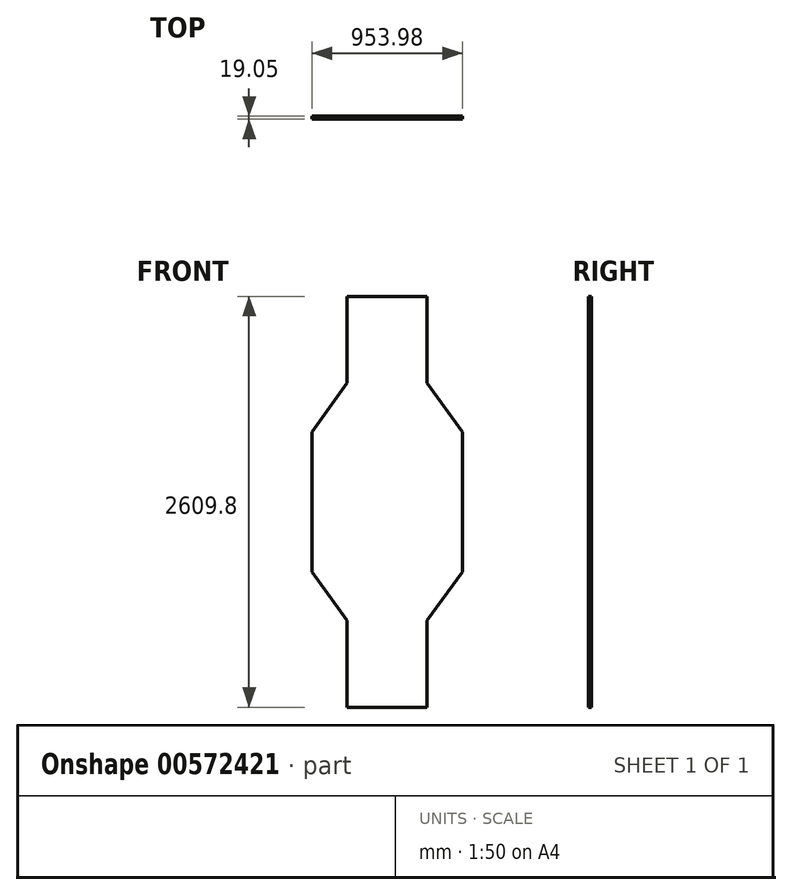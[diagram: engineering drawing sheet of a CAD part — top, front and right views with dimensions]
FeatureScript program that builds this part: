
annotation { "Feature Type Name" : "Feature", "Feature Type Description" : "" }
export const myFeature = defineFeature(function(context is Context, id is Id, definition is map)
    precondition{}
    {
        {
            var Q0;
            Q0=qCreatedBy(makeId("Front.planeOp"),FACE);
            var sketch = newSketch(context, id + "F0", { "sketchPlane" : qUnion([Q0])});
            skLineSegment(sketch, "E0", {"start": v(-515.56, -2037.32) * mm, "end": v(-292.57, -2346.25) * mm});
            skLineSegment(sketch, "E1", {"start": v(-292.57, -2346.25) * mm, "end": v(-292.57, -2897.72) * mm});
            skLineSegment(sketch, "E2", {"start": v(-292.57, -2897.72) * mm, "end": v(215.43, -2897.72) * mm});
            skLineSegment(sketch, "E3", {"start": v(215.43, -2897.72) * mm, "end": v(215.43, -2346.25) * mm});
            skPoint(sketch, "E4.startSnap0", {"position": v(-38.57, -2897.72) * mm});
            skLineSegment(sketch, "E5", {"start": v(-515.56, -2037.32) * mm, "end": v(-515.56, -1148.32) * mm});
            skLineSegment(sketch, "E6.MirrorCS", {"start": v(438.42, -2037.32) * mm, "end": v(438.42, -1148.32) * mm});
            skLineSegment(sketch, "E7.MirrorCS", {"start": v(438.42, -2037.32) * mm, "end": v(215.43, -2346.25) * mm});
            skLineSegment(sketch, "E8.MirrorCS", {"start": v(-515.56, -1148.32) * mm, "end": v(-292.57, -839.4) * mm});
            skLineSegment(sketch, "E9.MirrorCS", {"start": v(-292.57, -839.4) * mm, "end": v(-292.57, -287.92) * mm});
            skLineSegment(sketch, "E10.MirrorCS", {"start": v(215.43, -287.92) * mm, "end": v(215.43, -839.4) * mm});
            skLineSegment(sketch, "E11.MirrorCS", {"start": v(438.42, -1148.32) * mm, "end": v(215.43, -839.4) * mm});
            skLineSegment(sketch, "E12.MirrorCS", {"start": v(-292.57, -287.92) * mm, "end": v(215.43, -287.92) * mm});
            skSolve(sketch);
        }
        {
            var Q0;
            Q0 = qSketchRegion(id + "F0", true);
            extrude(context, id + "F1", {"entities" : qUnion([Q0]), "depth" : 19.05 * mm, "offsetDistance" : 25.4 * mm});
        }
        {
            var Q0;
            Q0=makeQuery(id+"F1.opExtrude","CAP_FACE",FACE,{"disambiguationData":[OSD([sQuery(id+"F0.wireOp",EDGE,"1gYgAiCd-tKT6-CdCx-Bodn-gtMO4Fr0BlfB"),sQuery(id+"F0.wireOp",EDGE,"YhjFyNPL-9biV-30GM-sShk-LnrCUCd5zFJC"),sQuery(id+"F0.wireOp",EDGE,"zzCJUBDA-PTzm-Nl60-ThWm-cnwSBQVinKBe"),sQuery(id+"F0.wireOp",EDGE,"QprXdcmA-9pbR-WBdM-V3ZM-AzTpjsBwY1Ps"),sQuery(id+"F0.wireOp",EDGE,"EYKvA0L6-KcQO-ryMO-VT9P-eRiES5l3jEc2"),sQuery(id+"F0.wireOp",EDGE,"E0"),sQuery(id+"F0.wireOp",EDGE,"7f6351c9-1889-4dda-90aa-f4ec030e5b050.MirrorCS"),sQuery(id+"F0.wireOp",EDGE,"8d60c9d0-adcc-46f1-8f2c-e5bed3e752a90.MirrorCS"),sQuery(id+"F0.wireOp",EDGE,"62c800c0-f48d-439d-b27b-761d792508fe0.MirrorCS"),sQuery(id+"F0.wireOp",EDGE,"E1"),sQuery(id+"F0.wireOp",EDGE,"E2"),sQuery(id+"F0.wireOp",EDGE,"E3"),sQuery(id+"F0.wireOp",EDGE,"pntoPswC-9uBv-hhwa-N1rV-Oz9da07gNBbK"),sQuery(id+"F0.wireOp",EDGE,"y0rVRHuu-dtnu-b4MY-6Hsp-9umWjWTruZ86"),sQuery(id+"F0.wireOp",EDGE,"bqmGCh54-uUi1-fcCV-GfKT-UgZ2a4ml20oo"),sQuery(id+"F0.wireOp",EDGE,"RfSjH4Rw-j5p4-9Kxe-vEWC-OOmDFJAFDaFd"),sQuery(id+"F0.wireOp",EDGE,"s2CET4yi-FVad-21pN-L7B5-SppDwabpdP4V"),sQuery(id+"F0.wireOp",EDGE,"t1X36nD7-NNLE-hOZJ-yRLO-hL51T7JqpywO")])],"isStart":false});
            var sketch = newSketch(context, id + "F2", { "sketchPlane" : qUnion([Q0])});
            skLineSegment(sketch, "E13", {"start": v(0, -359.94) * mm, "end": v(-124.04, -359.94) * mm});
            skLineSegment(sketch, "E14", {"start": v(-124.04, -359.94) * mm, "end": v(0, -359.94) * mm});
            skLineSegment(sketch, "E15", {"start": v(0, -359.94) * mm, "end": v(124.88, -359.94) * mm});
            skLineSegment(sketch, "E16", {"start": v(124.88, -2544.34) * mm, "end": v(-124.04, -2544.34) * mm});
            skLineSegment(sketch, "E17", {"start": v(378.88, -867.94) * mm, "end": v(378.88, -1121.94) * mm});
            skLineSegment(sketch, "E18", {"start": v(378.88, -1121.94) * mm, "end": v(124.88, -1121.94) * mm});
            skLineSegment(sketch, "E19", {"start": v(124.88, -1121.94) * mm, "end": v(124.88, -1325.14) * mm});
            skLineSegment(sketch, "E20", {"start": v(124.88, -1325.14) * mm, "end": v(378.88, -1325.14) * mm});
            skLineSegment(sketch, "E21", {"start": v(378.88, -1325.14) * mm, "end": v(378.88, -1579.14) * mm});
            skLineSegment(sketch, "E22", {"start": v(378.88, -1579.14) * mm, "end": v(124.88, -1579.14) * mm});
            skLineSegment(sketch, "E23", {"start": v(124.88, -1782.34) * mm, "end": v(378.88, -1782.34) * mm});
            skLineSegment(sketch, "E24", {"start": v(378.88, -1782.34) * mm, "end": v(378.88, -2036.34) * mm});
            skLineSegment(sketch, "E25", {"start": v(378.88, -2036.34) * mm, "end": v(124.88, -2036.34) * mm});
            skLineSegment(sketch, "E26.MirrorCS", {"start": v(-124.83, -867.94) * mm, "end": v(-378.83, -867.94) * mm});
            skLineSegment(sketch, "E27.MirrorCS", {"start": v(-378.83, -867.94) * mm, "end": v(-378.83, -1121.94) * mm});
            skLineSegment(sketch, "E28.MirrorCS", {"start": v(-378.83, -1121.94) * mm, "end": v(-124.83, -1121.94) * mm});
            skLineSegment(sketch, "E29.MirrorCS", {"start": v(-124.83, -1325.14) * mm, "end": v(-378.83, -1325.14) * mm});
            skLineSegment(sketch, "E30.MirrorCS", {"start": v(-378.83, -1325.14) * mm, "end": v(-378.83, -1579.14) * mm});
            skLineSegment(sketch, "E31.MirrorCS", {"start": v(-378.83, -1579.14) * mm, "end": v(-124.83, -1579.14) * mm});
            skLineSegment(sketch, "E32.MirrorCS", {"start": v(-124.83, -1782.34) * mm, "end": v(-378.83, -1782.34) * mm});
            skLineSegment(sketch, "E33.MirrorCS", {"start": v(-378.83, -1782.34) * mm, "end": v(-378.83, -2036.34) * mm});
            skLineSegment(sketch, "E34.MirrorCS", {"start": v(-379.73, -2036.34) * mm, "end": v(-125.73, -2036.34) * mm});
            skLineSegment(sketch, "E35", {"start": v(-124.83, -867.94) * mm, "end": v(-124.04, -359.94) * mm});
            skLineSegment(sketch, "E36", {"start": v(124.88, -867.94) * mm, "end": v(124.88, -359.94) * mm});
            skLineSegment(sketch, "E37", {"start": v(124.88, -2544.34) * mm, "end": v(124.88, -2036.34) * mm});
            skLineSegment(sketch, "E38", {"start": v(-124.04, -2544.34) * mm, "end": v(-125.73, -2036.34) * mm});
            skLineSegment(sketch, "E39", {"start": v(-124.83, -1782.34) * mm, "end": v(-124.83, -1579.14) * mm});
            skLineSegment(sketch, "E40", {"start": v(124.88, -1782.34) * mm, "end": v(124.88, -1579.14) * mm});
            skLineSegment(sketch, "E41", {"start": v(-124.83, -1325.14) * mm, "end": v(-124.83, -1121.94) * mm});
            skLineSegment(sketch, "E42", {"start": v(378.88, -867.94) * mm, "end": v(124.88, -867.94) * mm});
            skLineSegment(sketch, "E43.bottom", {"start": v(-124.04, -359.94) * mm, "end": v(124.88, -359.94) * mm});
            skLineSegment(sketch, "E43.top", {"start": v(-124.04, -2544.34) * mm, "end": v(124.88, -2544.34) * mm});
            skLineSegment(sketch, "E44.bottom", {"start": v(124.88, -1121.94) * mm, "end": v(378.88, -1121.94) * mm});
            skLineSegment(sketch, "E44.top", {"start": v(124.88, -867.94) * mm, "end": v(378.88, -867.94) * mm});
            skLineSegment(sketch, "E44.right", {"start": v(378.88, -1121.94) * mm, "end": v(378.88, -867.94) * mm});
            skLineSegment(sketch, "E45.top", {"start": v(124.88, -1579.14) * mm, "end": v(378.88, -1579.14) * mm});
            skLineSegment(sketch, "E46.top", {"start": v(124.88, -2036.34) * mm, "end": v(378.88, -2036.34) * mm});
            skLineSegment(sketch, "E47.bottom", {"start": v(-378.83, -1782.34) * mm, "end": v(-125.73, -1782.34) * mm});
            skLineSegment(sketch, "E47.top", {"start": v(-378.83, -2036.34) * mm, "end": v(-125.73, -2036.34) * mm});
            skLineSegment(sketch, "E48.bottom", {"start": v(-378.83, -1325.14) * mm, "end": v(-124.83, -1325.14) * mm});
            skLineSegment(sketch, "E49.bottom", {"start": v(-378.83, -867.94) * mm, "end": v(-124.83, -867.94) * mm});
            skSolve(sketch);
        }
        {
            var Q0;
            Q0=sQuery(id+"F2.wireOp",EDGE,"E36");
            var Q1;
            Q1=sQuery(id+"F2.wireOp",EDGE,"E35");
            var Q2;
            Q2=sQuery(id+"F2.wireOp",EDGE,"E15");
            var Q3;
            Q3=sQuery(id+"F2.wireOp",EDGE,"E14");
            var Q4;
            Q4=sQuery(id+"F2.wireOp",EDGE,"E42");
            var Q5;
            Q5=sQuery(id+"F2.wireOp",EDGE,"E17");
            var Q6;
            Q6=sQuery(id+"F2.wireOp",EDGE,"E18");
            var Q7;
            Q7=sQuery(id+"F2.wireOp",EDGE,"E26.MirrorCS");
            var Q8;
            Q8=sQuery(id+"F2.wireOp",EDGE,"E27.MirrorCS");
            var Q9;
            Q9=sQuery(id+"F2.wireOp",EDGE,"E28.MirrorCS");
            var Q10;
            Q10=sQuery(id+"F2.wireOp",EDGE,"E41");
            var Q11;
            Q11=sQuery(id+"F2.wireOp",EDGE,"E19");
            var Q12;
            Q12=sQuery(id+"F2.wireOp",EDGE,"E20");
            var Q13;
            Q13=sQuery(id+"F2.wireOp",EDGE,"E29.MirrorCS");
            var Q14;
            Q14=sQuery(id+"F2.wireOp",EDGE,"E30.MirrorCS");
            var Q15;
            Q15=sQuery(id+"F2.wireOp",EDGE,"E31.MirrorCS");
            var Q16;
            Q16=sQuery(id+"F2.wireOp",EDGE,"E22");
            var Q17;
            Q17=sQuery(id+"F2.wireOp",EDGE,"E21");
            var Q18;
            Q18=sQuery(id+"F2.wireOp",EDGE,"E40");
            var Q19;
            Q19=sQuery(id+"F2.wireOp",EDGE,"E23");
            var Q20;
            Q20=sQuery(id+"F2.wireOp",EDGE,"E24");
            var Q21;
            Q21=sQuery(id+"F2.wireOp",EDGE,"E25");
            var Q22;
            Q22=sQuery(id+"F2.wireOp",EDGE,"E39");
            var Q23;
            Q23=sQuery(id+"F2.wireOp",EDGE,"E32.MirrorCS");
            var Q24;
            Q24=sQuery(id+"F2.wireOp",EDGE,"E33.MirrorCS");
            var Q25;
            Q25=sQuery(id+"F2.wireOp",EDGE,"E34.MirrorCS");
            var Q26;
            Q26=sQuery(id+"F2.wireOp",EDGE,"E38");
            var Q27;
            Q27=sQuery(id+"F2.wireOp",EDGE,"E37");
            var Q28;
            Q28=sQuery(id+"F2.wireOp",EDGE,"E16");
            var Q29;
            Q29=sQuery(id+"F2.wireOp",EDGE,"E49.right");
            extrude(context, id + "F3", {"bodyType" : ToolBodyType.SURFACE, "surfaceEntities" : qUnion([Q0, Q1, Q2, Q3, Q4, Q5, Q6, Q7, Q8, Q9, Q10, Q11, Q12, Q13, Q14, Q15, Q16, Q17, Q18, Q19, Q20, Q21, Q22, Q23, Q24, Q25, Q26, Q27, Q28, Q29]), "depth" : 38.1 * mm, "offsetDistance" : 25.4 * mm});
        }
    });
